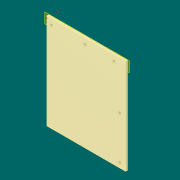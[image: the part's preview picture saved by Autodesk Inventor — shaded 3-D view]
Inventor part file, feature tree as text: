
AUTODESK INVENTOR PART (.ipt)
format: ipt  version: 2019 (Build 230136000, 136)  size: 187,392 bytes
history: native  units: mm
features: sketch x14, reference x13, extrude x10, other x3, plane x1
ambient origin geometry x8: Origin, YZ Plane, XZ Plane, XY Plane, X Axis, Y Axis, Z Axis, Center Point
bodies: Solid1 (feature_tree)
feature tree (41):
  plane  "Work Plane1"
  extrude  "Extrusion1"  Depth=2.0mm
  extrude  "Extrusion2"  Depth=2.5mm
  extrude  "Extrusion3"  Depth=2.5mm
  extrude  "Extrusion4"  Depth=8.0mm
  extrude  "Extrusion5"  Depth=8.0mm
  sketch  "Sketch6"  dims[d13=1.5mm d14=5.0mm d15=0.0mm]
  sketch  "Sketch7"  dims[d16=8.0mm d17=10.0mm]
  extrude  "Extrusion6"  Depth=5.0mm TaperAngle=0.0deg
  extrude  "Extrusion7"  Depth=10.0mm
  extrude  "Extrusion8"  Depth=5.0mm TaperAngle=0.0deg
  extrude  "Extrusion9"  Depth=8.0mm
  sketch  "Sketch12"  dims[d30=8.0mm d31=0.0mm]
  sketch  "Sketch13"  dims[d33=10.0mm]
  extrude  "Extrusion10"  Depth=1.5mm
  sketch  "Sketch1"  dims[d0=2.0mm d1=0.0mm d2=2.5mm]
  reference  "Reference1"
  reference  "Reference2"
  reference  "Reference3"
  reference  "Reference4"
  reference  "Reference5"
  reference  "Reference6"
  reference  "Reference7"
  reference  "Reference8"
  reference  "Reference9"
  sketch  "Sketch2"  dims[d3=2.5mm d4=2.5mm]
  sketch  "Sketch3"  dims[d5=2.5mm d6=2.5mm]
  reference  "Reference10"
  reference  "Reference11"
  sketch  "Sketch4"  dims[d7=2.0mm d8=0.0mm d9=8.0mm]
  sketch  "Sketch5"  dims[d10=10.0mm d11=8.0mm]
  reference  "Reference12"
  reference  "Reference13"
  sketch  "Sketch8"  dims[d19=1.5mm d20=5.0mm d21=0.0mm]
  sketch  "Sketch9"  dims[d22=10.0mm d23=8.0mm]
  sketch  "Sketch10"  dims[d25=1.5mm d27=1.5mm]
  sketch  "Sketch11"  dims[d28=5.0mm d29=0.0mm]
  sketch  "Sketch14"  dims[d34=8.0mm d35=10.0mm d38=8.0mm d39=0.0mm d40=8.0mm d41=0.0mm d42=15.0mm d43=8.0mm d44=10.0mm d45=8.0mm d46=0.0mm d50=1.5mm d51=8.0mm d52=0.0mm]
  other  "Ensamblaje Reloj LCD 16x2.iam"
  other  "Down:1"
  other  "Before:1"
